# Revit family: Sink-Top_Mount-Kitchen-KOHLER-PURIST-K-45811T
name_source: partatom
category: Plumbing Fixtures
revit_build: Autodesk Revit 2017 (Build: 20160225_1515(x64)
units: mm (PartAtom-declared; Revit-internal decimal feet)

## family parameters
Cut with Voids When Loaded = No
Host = Face
OmniClass Number = 23.31.13.00
OmniClass Title = Sinks
Part Type = Normal
Room Calculation Point = No
Round Connector Dimension = Use Diameter
Shared = No

## types (2) — shared parameters
ADA Compliant = No
Assembly Code = D2010400
CW Connection = No
Cold Water Inlet = Cold Water Inlet
Date Modified = 11/10/2020
Default Elevation = 36"
Drain Included = Yes
Finish = Kohler-Metal-NA-Stainless_Steel_Wire_Drawing
HW Connection = No
Height = 8 1/8"
Hot Water Inlet = Hot Water Inlet
Length = 18 1/2"
Manufacturer = KOHLER Co.
Master Format 2014 = 22 41 16
Master Format 2014 Name = Residential Lavatories and Sinks
Material = Stainless steel
Product Name = PURIST
URL = http://www.kohler.com.cn
Vent Connection = No
Waste Connection = Yes
Waste Water Outlet1 = Waste Water Outlet1
Waste Water Outlet2 = Waste Water Outlet2
WaterSense Certified = No
Width = 33 1/16"

## per-type parameters (varying)
| type | 2FD | 2RD | Description | Model | Type |
| 2FD,NA- Stainless steel wire drawing | Yes | No | LM SR SINK,2FD,NA | K-45811T-2FD-NA | 1 |
| 2RD, NA- Stainless steel wire drawing | No | Yes | LM SR SINK,2RD,NA | K-45811T-2RD-NA | 2 |

## geometry (parser evidence)
native form markers: Sweep x5
no freeform markers — native parametric forms only
